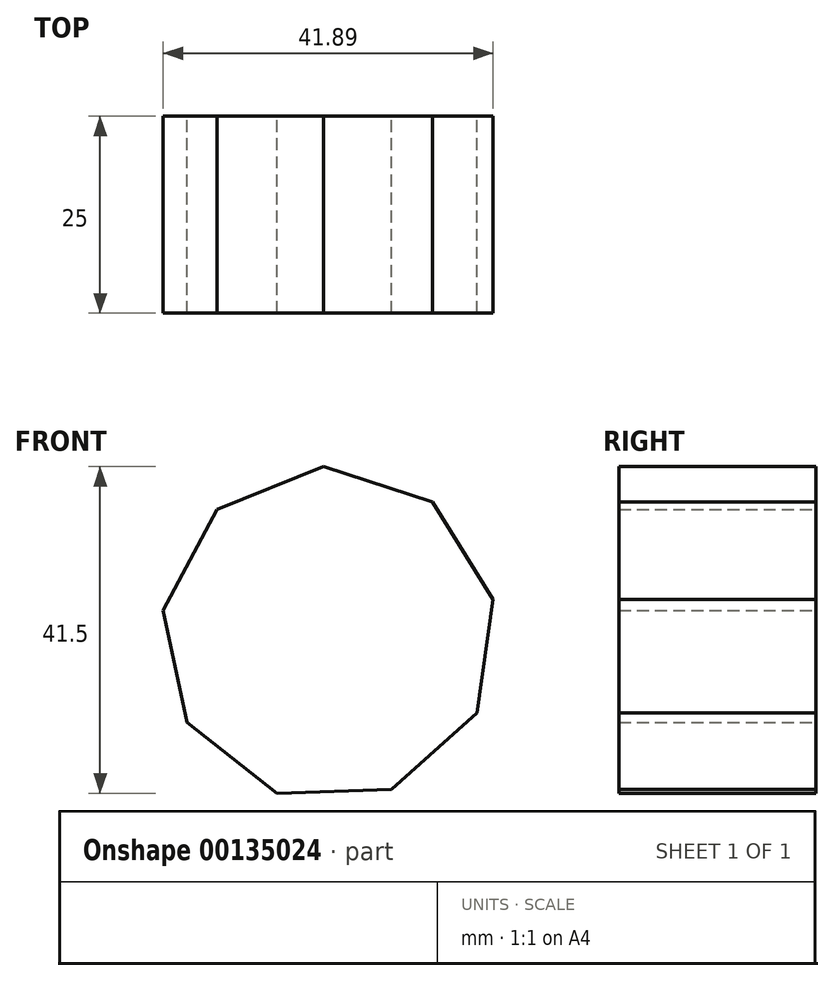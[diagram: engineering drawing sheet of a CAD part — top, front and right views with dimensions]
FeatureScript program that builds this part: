
annotation { "Feature Type Name" : "Feature", "Feature Type Description" : "" }
export const myFeature = defineFeature(function(context is Context, id is Id, definition is map)
    precondition{}
    {
        {
            var Q0;
            Q0=qCreatedBy(makeId("Front.planeOp"),FACE);
            var sketch = newSketch(context, id + "F0", { "sketchPlane" : qUnion([Q0])});
            skCircle(sketch, "E0.cCircle", {"center": v(0, 0) * mm, "radius": 20 * mm, "construction": true});
            skLineSegment(sketch, "E0.0", {"start": v(-14.22, 15.83) * mm, "end": v(-0.72, 21.27) * mm});
            skLineSegment(sketch, "E0.1", {"start": v(-0.72, 21.27) * mm, "end": v(13.12, 16.76) * mm});
            skLineSegment(sketch, "E0.2", {"start": v(13.12, 16.76) * mm, "end": v(20.82, 4.4) * mm});
            skLineSegment(sketch, "E0.3", {"start": v(20.82, 4.4) * mm, "end": v(18.78, -10.01) * mm});
            skLineSegment(sketch, "E0.4", {"start": v(18.78, -10.01) * mm, "end": v(7.95, -19.74) * mm});
            skLineSegment(sketch, "E0.5", {"start": v(7.95, -19.74) * mm, "end": v(-6.6, -20.23) * mm});
            skLineSegment(sketch, "E0.6", {"start": v(-6.6, -20.23) * mm, "end": v(-18.06, -11.26) * mm});
            skLineSegment(sketch, "E0.7", {"start": v(-18.06, -11.26) * mm, "end": v(-21.07, 2.99) * mm});
            skLineSegment(sketch, "E0.8", {"start": v(-21.07, 2.99) * mm, "end": v(-14.22, 15.83) * mm});
            skPoint(sketch, "E0.0.midPoint", {"position": v(-7.47, 18.55) * mm});
            skSolve(sketch);
        }
        {
            var Q0;
            Q0=makeQuery(id+"F0.imprint","IMPRINT",FACE,{"disambiguationData":[TD([[makeQuery(id+"F0.imprint","IMPRINT",EDGE,{"derivedFrom":sQuery(id+"F0.wireOp",EDGE,"E0.0")}),-1.0]])]});
            extrude(context, id + "F1", {"entities" : qUnion([Q0]), "depth" : 25 * mm});
        }
    });
